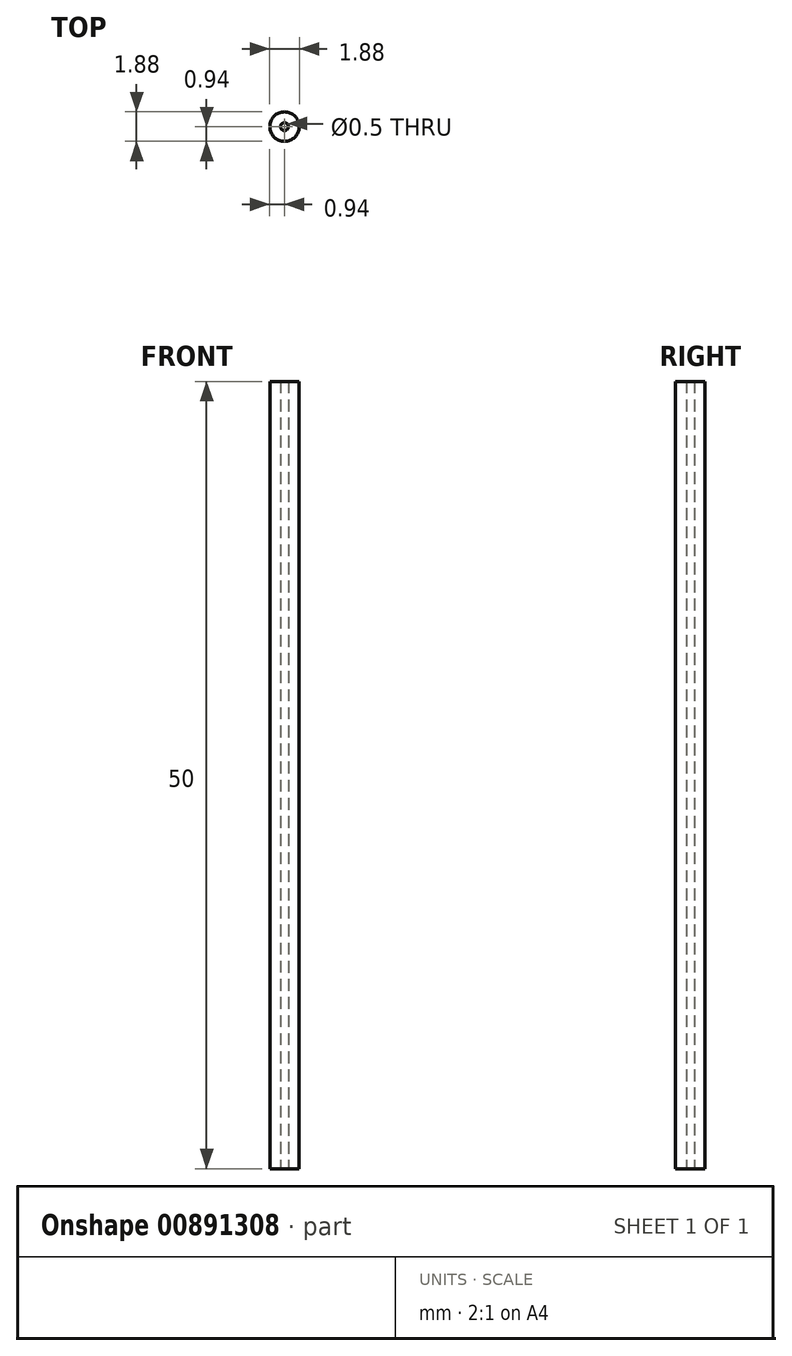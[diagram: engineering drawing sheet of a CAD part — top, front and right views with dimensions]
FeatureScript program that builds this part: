
annotation { "Feature Type Name" : "Feature", "Feature Type Description" : "" }
export const myFeature = defineFeature(function(context is Context, id is Id, definition is map)
    precondition{}
    {
        {
            var Q0;
            Q0=qCreatedBy(makeId("Top.planeOp"),FACE);
            var sketch = newSketch(context, id + "F0", { "sketchPlane" : qUnion([Q0])});
            skCircle(sketch, "E0", {"center": v(0, 0) * mm, "radius": 0.94 * mm});
            skCircle(sketch, "E1", {"center": v(0, 0) * mm, "radius": 0.25 * mm});
            skSolve(sketch);
        }
        {
            var Q0;
            Q0=makeQuery(id+"F0.imprint","IMPRINT",FACE,{"disambiguationData":[TD([[makeQuery(id+"F0.imprint","IMPRINT",EDGE,{"derivedFrom":sQuery(id+"F0.wireOp",EDGE,"E0")}),1.0]])]});
            extrude(context, id + "F1", {"entities" : qUnion([Q0]), "depth" : 50 * mm, "offsetDistance" : 25.4 * mm});
        }
    });
